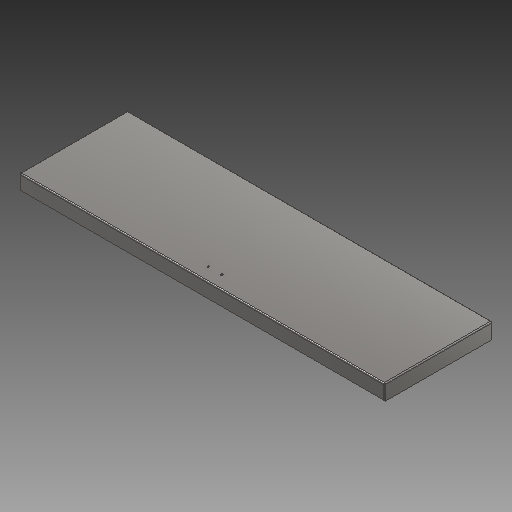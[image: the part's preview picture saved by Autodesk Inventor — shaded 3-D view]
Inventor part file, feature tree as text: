
AUTODESK INVENTOR PART (.ipt)
format: ipt  version: 2017 (Build 210142000, 142)  size: 226,304 bytes
history: native  units: mm
features: sheet_metal_op x7, other x6, sketch x4, reference x2, extrude x1
ambient origin geometry x8: Origin, YZ Plane, XZ Plane, XY Plane, X Axis, Y Axis, Z Axis, Center Point
bodies: Solid1 (feature_tree)
feature tree (20):
  sheet_metal_op  "Face1"
  sheet_metal_op  "Flange1"
  sheet_metal_op  "Flange2"
  extrude  "Extrusion1"  Depth=278.299mm
  sketch  "Sketch1"  dims[d0=936.598mm d1=278.299mm]
  other  "Plate1"
  sketch  "Sketch2"  dims[d2=1.5mm]
  other  "Plate2"
  sheet_metal_op  "Bend1"
  sheet_metal_op  "Corner1"
  sketch  "Sketch3"  dims[d3=1.5mm]
  other  "Plate3"
  sheet_metal_op  "Bend2"
  sheet_metal_op  "Corner2"
  sketch  "Sketch4"  dims[d4=0.75mm d5=3.0mm d6=1.5mm d7=40.0mm d8=90.0deg d9=1.5mm d10=6.0mm d11=1.5mm d12=1.5mm d13=1.5mm d14=0.75mm d15=3.0mm d16=1.5mm d17=10.0mm d18=90.0deg d19=1.5mm d20=6.0mm d21=1.5mm d22=1.5mm d23=10.0mm d24=0.0mm]
  reference  "Reference1"
  reference  "Reference2"
  other  "Definition1"
  other  "Bancada de Lavagem Mãos - 1150 x 370 x 900h.iam"
  other  "Batente batoque Inferior:1"
